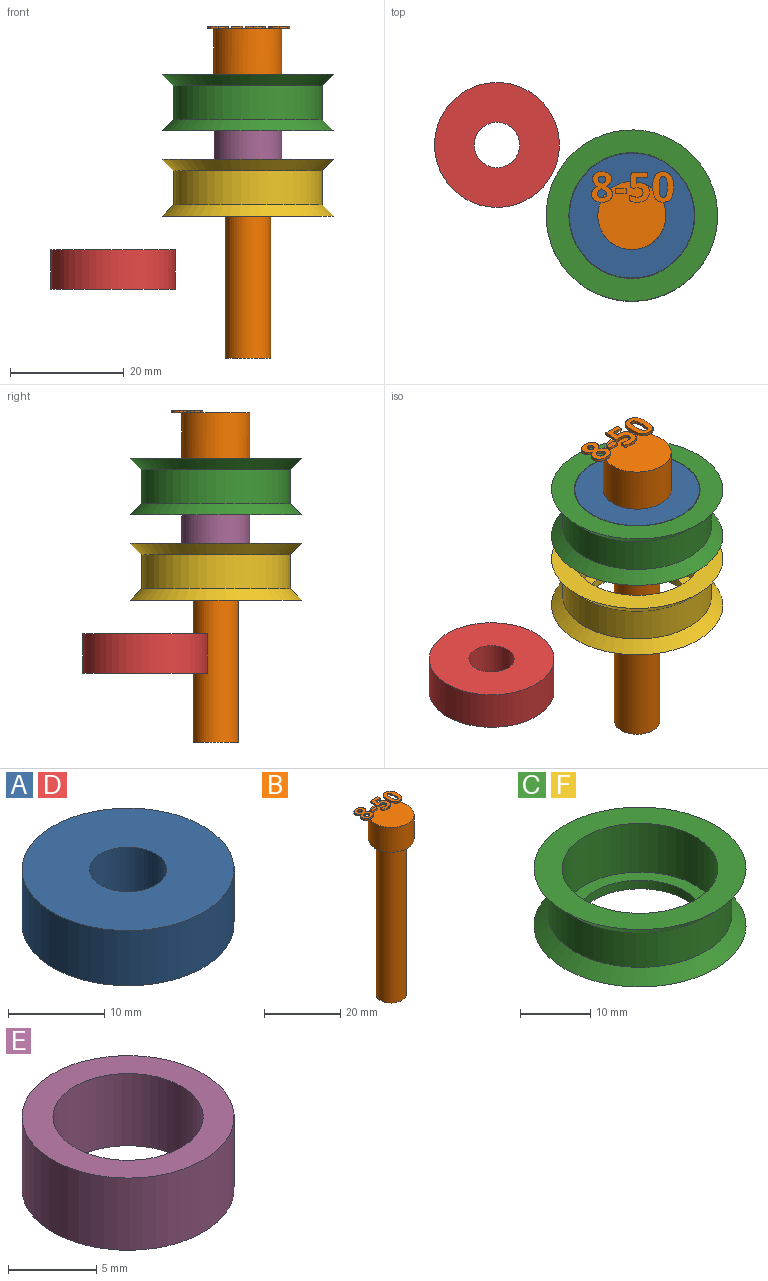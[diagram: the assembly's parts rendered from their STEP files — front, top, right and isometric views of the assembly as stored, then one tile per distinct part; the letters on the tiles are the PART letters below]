
ASSEMBLY  parts=6 mates=4
PART A: 4 faces, bbox 22x22x7 mm
  f0: cylinder r=4mm len=8mm, axis (0,0,-1), area 175.9mm2, adj f2,f3
  f1: cylinder r=11mm len=22mm, axis (0,0,-1), area 483.8mm2, adj f2,f3
  f2: plane 22x22mm, normal (0,0,1), area 329.9mm2, adj f0,f1
  f3: plane 22x22mm, normal (0,0,-1), area 329.9mm2, adj f0,f1
PART B: 86 faces, bbox 14.5x13.7x58.5 mm
  f0: plane 12x12mm, normal (0,0,1), area 99.4mm2, adj f5,f22,f23,f24,f25,f26,f40,f41
  f1: plane 1x0.26mm, normal (0,0,1), area 0.1mm2, adj f5,f46,f47,f48,f49
  f2: plane 0.85x0.68mm, normal (0,0,1), area 0.2mm2, adj f5,f29,f30,f31
  f3: cylinder r=4mm len=50mm, axis (0,0,-1), area 1256.6mm2, adj f4,f6
  f4: plane 8x8mm, normal (0,0,-1), area 50.3mm2, adj f3
  f5: cylinder r=6mm len=12mm, axis (0,0,-1), area 301.6mm2, adj f0,f1,f2,f6,f39,f45,f67,f85
  f6: plane 12x12mm, normal (0,0,-1), area 62.8mm2, adj f3,f5
  f7: extruded ~0.5x0.46mm, area 0.2mm2, adj f8,f37,f38,f39
  f8: extruded ~0.5x0.46mm, area 0.2mm2, adj f7,f9,f38,f39
  f9: extruded ~0.5x0.39mm, area 0.2mm2, adj f8,f10,f38,f39
  f10: extruded ~0.5x0.4mm, area 0.2mm2, adj f9,f11,f38,f39
  f11: extruded ~0.5x0.49mm, area 0.3mm2, adj f10,f12,f38,f39
  f12: extruded ~0.5x0.5mm, area 0.3mm2, adj f11,f13,f38,f39
  f13: extruded ~0.5x0.39mm, area 0.2mm2, adj f12,f37,f38,f39
  f14: extruded ~1.22x0.5mm, area 0.6mm2, adj f15,f35,f38,f39
  f15: extruded ~1.22x0.5mm, area 0.6mm2, adj f14,f16,f38,f39
  f16: extruded ~0.91x0.5mm, area 0.5mm2, adj f15,f17,f38,f39
  f17: extruded ~0.71x0.5mm, area 0.4mm2, adj f16,f18,f38,f39
  f18: extruded ~0.65x0.61mm, area 0.4mm2, adj f17,f19,f38,f39
  f19: extruded ~0.77x0.62mm, area 0.5mm2, adj f18,f20,f38,f39
  f20: extruded ~0.8x0.5mm, area 0.4mm2, adj f19,f21,f38,f39
  f21: extruded ~1.04x0.5mm, area 0.6mm2, adj f20,f22,f38,f39
  f22: extruded ~1.36x0.5mm, area 0.7mm2, adj f0,f21,f23,f38,f39
  f23: extruded ~1.33x0.5mm, area 0.7mm2, adj f0,f22,f24,f38
  f24: extruded ~1.04x0.51mm, area 0.6mm2, adj f0,f23,f25,f38
  f25: extruded ~0.75x0.5mm, area 0.4mm2, adj f0,f24,f26,f38
  f26: extruded ~0.85x0.66mm, area 0.5mm2, adj f0,f25,f27,f38,f39
  f27: extruded ~0.72x0.56mm, area 0.5mm2, adj f26,f28,f38,f39
  f28: extruded ~0.72x0.5mm, area 0.4mm2, adj f27,f35,f38,f39
  f29: extruded ~0.5x0.45mm, area 0.3mm2, adj f2,f30,f36,f38,f39
  f30: extruded ~0.5x0.47mm, area 0.3mm2, adj f2,f29,f31,f38
  f31: extruded ~0.62x0.5mm, area 0.3mm2, adj f2,f30,f32,f38,f39
  f32: extruded ~0.59x0.5mm, area 0.3mm2, adj f31,f33,f38,f39
  f33: extruded ~0.5x0.48mm, area 0.3mm2, adj f32,f34,f38,f39
  f34: extruded ~0.89x0.77mm, area 0.6mm2, adj f33,f36,f38,f39
  f35: extruded ~0.93x0.5mm, area 0.5mm2, adj f14,f28,f38,f39
  f36: extruded ~0.66x0.5mm, area 0.4mm2, adj f29,f34,f38,f39
  f37: extruded ~0.5x0.39mm, area 0.2mm2, adj f7,f13,f38,f39
  f38: plane 5.4x3.69mm, normal (0,0,1), area 12.7mm2, adj f7,f8,f9,f10,f11,f12,f13,f14
  f39: plane 5.4x3.53mm, normal (0,0,-1), area 10.2mm2, adj f5,f7,f8,f9,f10,f11,f12,f13
  f40: plane 0.9x0.5mm, normal (-1,0,0), area 0.4mm2, adj f0,f41,f43,f44
  f41: plane 1.93x0.5mm, normal (0,-1,0), area 1mm2, adj f0,f40,f42,f44
  f42: plane 0.9x0.5mm, normal (1,0,0), area 0.4mm2, adj f0,f41,f43,f44
  f43: plane 1.93x0.5mm, normal (0,1,0), area 1mm2, adj f0,f40,f42,f44
  f44: plane 1.93x0.9mm, normal (0,0,1), area 1.7mm2, adj f40,f41,f42,f43
  f45: plane 0.76x0.31mm, normal (0,0,-1), area 0mm2, adj f5,f46
  f46: extruded ~1.21x0.5mm, area 0.7mm2, adj f0,f1,f45,f47,f65,f66
  f47: extruded ~0.54x0.5mm, area 0.3mm2, adj f1,f46,f48,f66
  f48: plane 0.5x0.13mm, normal (-0.2,0.98,0), area 0.1mm2, adj f1,f47,f49,f66
  f49: plane 1.03x0.5mm, normal (1,-0.09,0), area 0.5mm2, adj f1,f48,f50,f66,f67
  f50: plane 1.88x0.5mm, normal (0,-1,0), area 0.9mm2, adj f49,f51,f66,f67
  f51: plane 0.94x0.5mm, normal (1,0,0), area 0.5mm2, adj f50,f52,f66,f67
  f52: plane 2.85x0.5mm, normal (0,1,0), area 1.4mm2, adj f51,f53,f66,f67
  f53: plane 2.68x0.5mm, normal (-1,0.07,0), area 1.3mm2, adj f0,f52,f54,f66,f67
  f54: plane 0.5x0.44mm, normal (-0.47,-0.88,0), area 0.3mm2, adj f0,f53,f55,f66
  f55: extruded ~0.5x0.37mm, area 0.2mm2, adj f0,f54,f56,f66
  f56: extruded ~0.5x0.42mm, area 0.2mm2, adj f0,f55,f57,f66
  f57: extruded ~1.05x0.8mm, area 0.8mm2, adj f0,f56,f58,f66
  f58: extruded ~1.02x0.83mm, area 0.8mm2, adj f0,f57,f59,f66
  f59: extruded ~0.72x0.5mm, area 0.4mm2, adj f0,f58,f60,f66
  f60: extruded ~0.66x0.5mm, area 0.4mm2, adj f0,f59,f61,f66
  f61: plane 0.96x0.5mm, normal (-1,0,0), area 0.5mm2, adj f0,f60,f62,f66
  f62: extruded ~1.42x0.5mm, area 0.7mm2, adj f0,f61,f63,f66
  f63: extruded ~1.55x0.5mm, area 0.8mm2, adj f0,f62,f64,f66
  f64: extruded ~1.36x0.54mm, area 0.8mm2, adj f0,f63,f65,f66
  f65: extruded ~1.17x0.5mm, area 0.6mm2, adj f0,f46,f64,f66
  f66: plane 5.33x3.51mm, normal (0,0,1), area 10.9mm2, adj f46,f47,f48,f49,f50,f51,f52,f53
  f67: plane 2.97x1.71mm, normal (0,0,-1), area 3.5mm2, adj f5,f49,f50,f51,f52,f53
  f68: extruded ~1.39x0.5mm, area 0.7mm2, adj f69,f83,f84,f85
  f69: extruded ~1.39x0.5mm, area 0.7mm2, adj f68,f70,f84,f85
  f70: extruded ~0.56x0.5mm, area 0.4mm2, adj f69,f71,f84,f85
  f71: extruded ~0.56x0.5mm, area 0.4mm2, adj f70,f72,f84,f85
  f72: extruded ~1.39x0.5mm, area 0.7mm2, adj f71,f73,f84,f85
  f73: extruded ~1.38x0.5mm, area 0.7mm2, adj f72,f74,f84,f85
  f74: extruded ~0.56x0.5mm, area 0.4mm2, adj f73,f83,f84,f85
  f75: extruded ~2.04x0.5mm, area 1.1mm2, adj f76,f82,f84,f85
  f76: extruded ~2.02x0.5mm, area 1.1mm2, adj f75,f77,f84,f85
  f77: extruded ~1.38x0.69mm, area 0.8mm2, adj f76,f78,f84,f85
  f78: extruded ~1.38x0.66mm, area 0.8mm2, adj f77,f79,f84,f85
  f79: extruded ~2.05x0.5mm, area 1.1mm2, adj f78,f80,f84,f85
  f80: extruded ~2.02x0.5mm, area 1mm2, adj f0,f79,f81,f84,f85
  f81: extruded ~1.37x0.68mm, area 0.8mm2, adj f0,f80,f82,f84
  f82: extruded ~1.39x0.66mm, area 0.8mm2, adj f0,f75,f81,f84,f85
  f83: extruded ~0.56x0.5mm, area 0.4mm2, adj f68,f74,f84,f85
  f84: plane 5.41x3.68mm, normal (0,0,1), area 12.1mm2, adj f68,f69,f70,f71,f72,f73,f74,f75
  f85: plane 5.41x3.68mm, normal (0,0,-1), area 10.3mm2, adj f5,f68,f69,f70,f71,f72,f73,f74
PART C: 8 faces, bbox 30.2x30.2x10 mm
  f0: plane 30.2x30.2mm, normal (0,0,1), area 329.2mm2, adj f1,f7
  f1: cylinder r=11.1mm len=22.2mm, axis (0,0,-1), area 592.8mm2, adj f0,f2
  f2: plane 22.2x22.2mm, normal (0,0,1), area 126.9mm2, adj f1,f3
  f3: cylinder r=9.1mm len=18.2mm, axis (0,0,-1), area 85.8mm2, adj f2,f4
  f4: plane 30.2x30.2mm, normal (0,0,-1), area 456.2mm2, adj f3,f5
  f5: cone r=13.1mm half-angle=45deg, axis (0,0,-1), area 250.6mm2, adj f4,f6
  f6: cylinder r=13.1mm len=26.2mm, axis (0,0,-1), area 493.9mm2, adj f5,f7
  f7: cone r=15.1mm half-angle=45deg, axis (0,0,1), area 250.6mm2, adj f0,f6
PART D: same geometry as A
PART E: 4 faces, bbox 12x12x5 mm
  f0: cylinder r=4.25mm len=8.5mm, axis (0,0,-1), area 133.5mm2, adj f2,f3
  f1: cylinder r=6mm len=12mm, axis (0,0,-1), area 188.5mm2, adj f2,f3
  f2: plane 12x12mm, normal (0,0,1), area 56.4mm2, adj f0,f1
  f3: plane 12x12mm, normal (0,0,-1), area 56.4mm2, adj f0,f1
PART F: same geometry as C
PLACE A t=(23.78,-12.5,30.9)mm
PLACE B t=(23.78,-12.5,-12.1)mm
PLACE C t=(23.78,-12.5,33.1)mm
PLACE D at identity
PLACE E rot(axis=(1,0,0),180deg) t=(23.78,-12.5,27.9)mm
PLACE F t=(23.78,-12.5,18.1)mm
MATE fastened E.f0 <-> F.f1  axis (0,0,1) through (23.78,-12.5,22.9)mm
MATE fastened A.f0 <-> C.f1  axis (0,0,1) through (23.78,-12.5,37.9)mm
MATE fastened C.f1 <-> F.f1  axis (0,0,-1) through (23.78,-12.5,27.9)mm
MATE fastened B.f3 <-> C.f1  axis (0,0,-1) through (23.78,-12.5,37.9)mm
